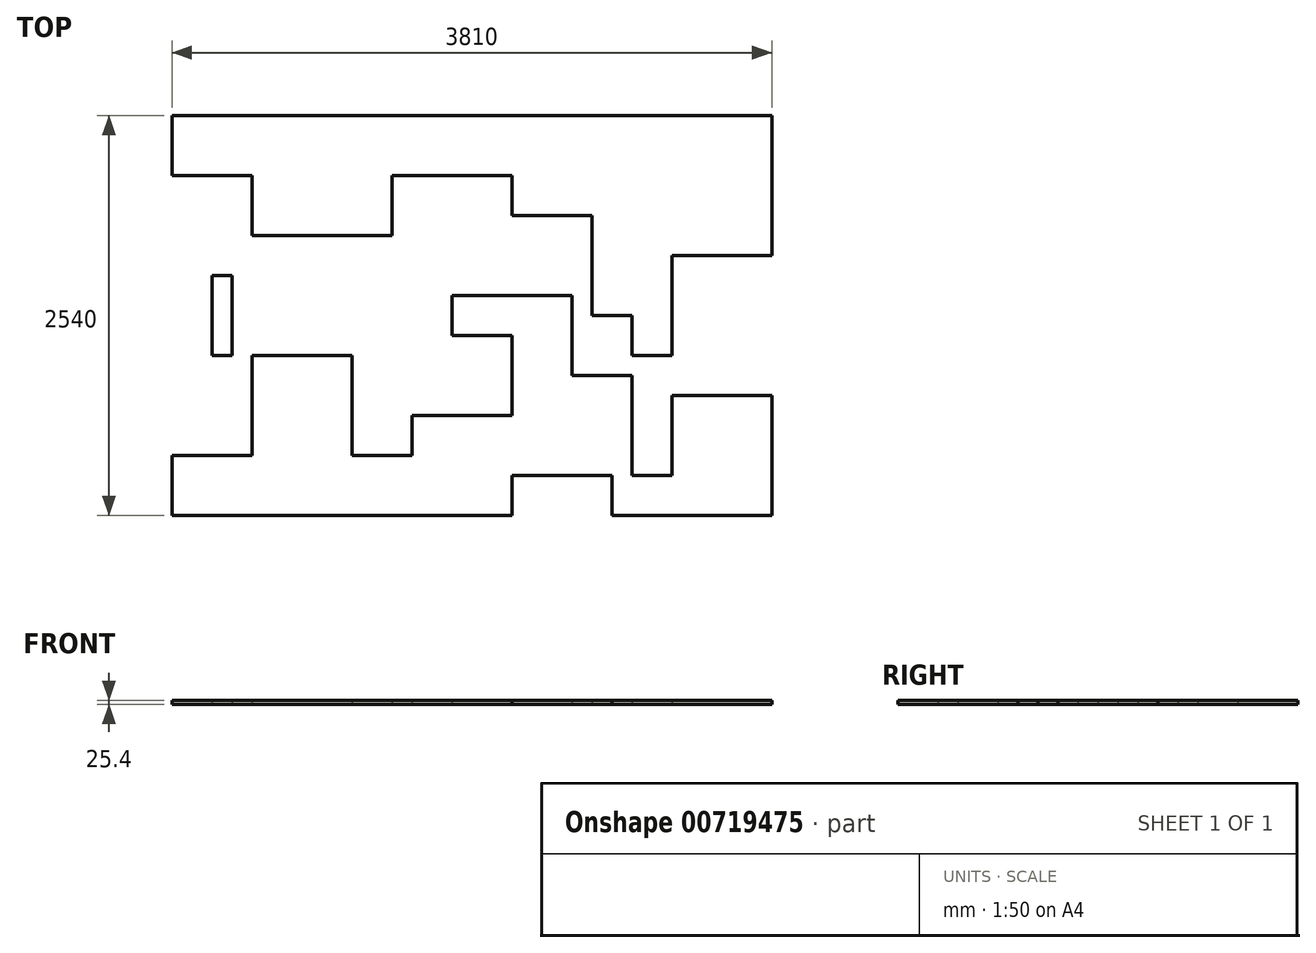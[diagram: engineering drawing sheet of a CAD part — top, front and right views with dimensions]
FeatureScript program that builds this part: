
annotation { "Feature Type Name" : "Feature", "Feature Type Description" : "" }
export const myFeature = defineFeature(function(context is Context, id is Id, definition is map)
    precondition{}
    {
        {
            var Q0;
            Q0=qCreatedBy(makeId("Top.planeOp"),FACE);
            var sketch = newSketch(context, id + "F0", { "sketchPlane" : qUnion([Q0])});
            skLineSegment(sketch, "E0", {"start": v(-1270, 1270) * mm, "end": v(-1270, -1270) * mm, "construction": true});
            skLineSegment(sketch, "E1", {"start": v(-1270, -1270) * mm, "end": v(2540, -1270) * mm, "construction": true});
            skLineSegment(sketch, "E2.0.2.0", {"start": v(889, -1016) * mm, "end": v(2540, -1016) * mm, "construction": true});
            skLineSegment(sketch, "E2.0.3.0", {"start": v(-1270, -889) * mm, "end": v(-762, -889) * mm, "construction": true});
            skLineSegment(sketch, "E2.0.8.0", {"start": v(-1270, -254) * mm, "end": v(-889, -254) * mm, "construction": true});
            skLineSegment(sketch, "E2.0.9.0", {"start": v(508, -127) * mm, "end": v(1270, -127) * mm, "construction": true});
            skLineSegment(sketch, "E2.0.10.0", {"start": v(-127, 0) * mm, "end": v(254, 0) * mm, "construction": true});
            skLineSegment(sketch, "E2.0.11.0", {"start": v(508, 127) * mm, "end": v(1270, 127) * mm, "construction": true});
            skLineSegment(sketch, "E2.0.12.0", {"start": v(-1016, 254) * mm, "end": v(-762, 254) * mm, "construction": true});
            skLineSegment(sketch, "E2.0.13.0", {"start": v(-762, 381) * mm, "end": v(508, 381) * mm, "construction": true});
            skLineSegment(sketch, "E2.0.14.0", {"start": v(-1270, 508) * mm, "end": v(508, 508) * mm, "construction": true});
            skLineSegment(sketch, "E2.0.17.0", {"start": v(-1270, 889) * mm, "end": v(-762, 889) * mm, "construction": true});
            skLineSegment(sketch, "E2.direction1", {"start": v(-1270, -1270) * mm, "end": v(-1244.6, -1270) * mm, "construction": true});
            skLineSegment(sketch, "E2.direction2", {"start": v(-1270, -1270) * mm, "end": v(-1270, -1143) * mm, "construction": true});
            skLineSegment(sketch, "E3.0.0.20", {"start": v(-1270, 1270) * mm, "end": v(2540, 1270) * mm, "construction": true});
            skLineSegment(sketch, "E4.4.0.0", {"start": v(-762, 1270) * mm, "end": v(-762, -1270) * mm, "construction": true});
            skLineSegment(sketch, "E4.9.0.0", {"start": v(-127, 1270) * mm, "end": v(-127, 508) * mm, "construction": true});
            skLineSegment(sketch, "E4.11.0.0", {"start": v(127, 1270) * mm, "end": v(127, 508) * mm, "construction": true});
            skLineSegment(sketch, "E4.14.0.0", {"start": v(508, 889) * mm, "end": v(508, -1270) * mm, "construction": true});
            skLineSegment(sketch, "E4.17.0.0", {"start": v(889, 1270) * mm, "end": v(889, 127) * mm, "construction": true});
            skLineSegment(sketch, "E4.direction1", {"start": v(-1270, -1270) * mm, "end": v(-1143, -1270) * mm, "construction": true});
            skLineSegment(sketch, "E5.0.20.0", {"start": v(1270, 635) * mm, "end": v(1270, -381) * mm, "construction": true});
            skLineSegment(sketch, "E6.0.21.0", {"start": v(1397, 1270) * mm, "end": v(1397, -254) * mm, "construction": true});
            skLineSegment(sketch, "E6.0.25.0", {"start": v(1905, 1270) * mm, "end": v(1905, -127) * mm, "construction": true});
            skLineSegment(sketch, "E6.0.28.0", {"start": v(2286, 381) * mm, "end": v(2286, -508) * mm, "construction": true});
            skLineSegment(sketch, "E6.0.30.0", {"start": v(2540, 1270) * mm, "end": v(2540, -1270) * mm, "construction": true});
            skLineSegment(sketch, "E7.bottom", {"start": v(-1270, 1270) * mm, "end": v(-762, 1270) * mm});
            skLineSegment(sketch, "E7.top", {"start": v(-1270, 889) * mm, "end": v(-762, 889) * mm});
            skLineSegment(sketch, "E7.left", {"start": v(-1270, 1270) * mm, "end": v(-1270, 889) * mm});
            skLineSegment(sketch, "E7.right", {"start": v(-762, 1270) * mm, "end": v(-762, 889) * mm});
            skLineSegment(sketch, "E8.bottom", {"start": v(-762, 1270) * mm, "end": v(-127, 1270) * mm});
            skLineSegment(sketch, "E8.top", {"start": v(-762, 508) * mm, "end": v(-127, 508) * mm});
            skLineSegment(sketch, "E8.left", {"start": v(-762, 1270) * mm, "end": v(-762, 508) * mm});
            skLineSegment(sketch, "E8.right", {"start": v(-127, 1270) * mm, "end": v(-127, 508) * mm});
            skLineSegment(sketch, "E9.bottom", {"start": v(-127, 762) * mm, "end": v(127, 762) * mm});
            skLineSegment(sketch, "E9.top", {"start": v(-127, 1270) * mm, "end": v(127, 1270) * mm});
            skLineSegment(sketch, "E9.left", {"start": v(-127, 762) * mm, "end": v(-127, 1270) * mm});
            skLineSegment(sketch, "E9.right", {"start": v(127, 762) * mm, "end": v(127, 1270) * mm});
            skLineSegment(sketch, "E10.bottom", {"start": v(127, 1270) * mm, "end": v(889, 1270) * mm});
            skLineSegment(sketch, "E10.top", {"start": v(127, 889) * mm, "end": v(889, 889) * mm});
            skLineSegment(sketch, "E10.left", {"start": v(127, 1270) * mm, "end": v(127, 889) * mm});
            skLineSegment(sketch, "E10.right", {"start": v(889, 1270) * mm, "end": v(889, 889) * mm});
            skLineSegment(sketch, "E11.bottom", {"start": v(889, 1270) * mm, "end": v(1397, 1270) * mm});
            skLineSegment(sketch, "E11.top", {"start": v(889, 635) * mm, "end": v(1397, 635) * mm});
            skLineSegment(sketch, "E11.left", {"start": v(889, 1270) * mm, "end": v(889, 635) * mm});
            skLineSegment(sketch, "E11.right", {"start": v(1397, 1270) * mm, "end": v(1397, 635) * mm});
            skLineSegment(sketch, "E12.bottom", {"start": v(508, 889) * mm, "end": v(127, 889) * mm});
            skLineSegment(sketch, "E12.top", {"start": v(508, 508) * mm, "end": v(127, 508) * mm});
            skLineSegment(sketch, "E12.left", {"start": v(508, 889) * mm, "end": v(508, 508) * mm});
            skLineSegment(sketch, "E12.right", {"start": v(127, 889) * mm, "end": v(127, 508) * mm});
            skLineSegment(sketch, "E13.bottom", {"start": v(889, 254) * mm, "end": v(508, 254) * mm});
            skLineSegment(sketch, "E13.top", {"start": v(889, 889) * mm, "end": v(508, 889) * mm});
            skLineSegment(sketch, "E13.left", {"start": v(889, 254) * mm, "end": v(889, 889) * mm});
            skLineSegment(sketch, "E13.right", {"start": v(508, 254) * mm, "end": v(508, 889) * mm});
            skLineSegment(sketch, "E14.bottom", {"start": v(1397, 889) * mm, "end": v(1905, 889) * mm});
            skLineSegment(sketch, "E14.top", {"start": v(1397, 1270) * mm, "end": v(1905, 1270) * mm});
            skLineSegment(sketch, "E14.left", {"start": v(1397, 889) * mm, "end": v(1397, 1270) * mm});
            skLineSegment(sketch, "E14.right", {"start": v(1905, 889) * mm, "end": v(1905, 1270) * mm});
            skLineSegment(sketch, "E15.bottom", {"start": v(1905, 1270) * mm, "end": v(2540, 1270) * mm});
            skLineSegment(sketch, "E15.top", {"start": v(1905, 381) * mm, "end": v(2540, 381) * mm});
            skLineSegment(sketch, "E15.left", {"start": v(1905, 1270) * mm, "end": v(1905, 381) * mm});
            skLineSegment(sketch, "E15.right", {"start": v(2540, 1270) * mm, "end": v(2540, 381) * mm});
            skLineSegment(sketch, "E16.top", {"start": v(1397, 0) * mm, "end": v(1905, 0) * mm});
            skLineSegment(sketch, "E16.left", {"start": v(1397, 889) * mm, "end": v(1397, 0) * mm});
            skLineSegment(sketch, "E16.right", {"start": v(1905, 889) * mm, "end": v(1905, 0) * mm});
            skLineSegment(sketch, "E17.bottom", {"start": v(1905, 381) * mm, "end": v(2286, 381) * mm});
            skLineSegment(sketch, "E17.top", {"start": v(1905, -254) * mm, "end": v(2286, -254) * mm});
            skLineSegment(sketch, "E17.left", {"start": v(1905, 381) * mm, "end": v(1905, -254) * mm});
            skLineSegment(sketch, "E17.right", {"start": v(2286, 381) * mm, "end": v(2286, -254) * mm});
            skLineSegment(sketch, "E18.bottom", {"start": v(2286, 381) * mm, "end": v(2540, 381) * mm});
            skLineSegment(sketch, "E18.top", {"start": v(2286, -508) * mm, "end": v(2540, -508) * mm});
            skLineSegment(sketch, "E18.left", {"start": v(2286, 381) * mm, "end": v(2286, -508) * mm});
            skLineSegment(sketch, "E18.right", {"start": v(2540, 381) * mm, "end": v(2540, -508) * mm});
            skLineSegment(sketch, "E19.bottom", {"start": v(2286, -254) * mm, "end": v(1651, -254) * mm});
            skLineSegment(sketch, "E19.top", {"start": v(2286, -508) * mm, "end": v(1651, -508) * mm});
            skLineSegment(sketch, "E19.left", {"start": v(2286, -254) * mm, "end": v(2286, -508) * mm});
            skLineSegment(sketch, "E19.right", {"start": v(1651, -254) * mm, "end": v(1651, -508) * mm});
            skLineSegment(sketch, "E20.bottom", {"start": v(2540, -508) * mm, "end": v(1905, -508) * mm});
            skLineSegment(sketch, "E20.top", {"start": v(2540, -1016) * mm, "end": v(1905, -1016) * mm});
            skLineSegment(sketch, "E20.left", {"start": v(2540, -508) * mm, "end": v(2540, -1016) * mm});
            skLineSegment(sketch, "E20.right", {"start": v(1905, -508) * mm, "end": v(1905, -1016) * mm});
            skLineSegment(sketch, "E21.bottom", {"start": v(2540, -1270) * mm, "end": v(2032, -1270) * mm});
            skLineSegment(sketch, "E21.top", {"start": v(2540, -1016) * mm, "end": v(2032, -1016) * mm});
            skLineSegment(sketch, "E21.left", {"start": v(2540, -1270) * mm, "end": v(2540, -1016) * mm});
            skLineSegment(sketch, "E21.right", {"start": v(2032, -1270) * mm, "end": v(2032, -1016) * mm});
            skLineSegment(sketch, "E22.bottom", {"start": v(1651, -508) * mm, "end": v(1905, -508) * mm});
            skLineSegment(sketch, "E22.top", {"start": v(1651, -1016) * mm, "end": v(1905, -1016) * mm});
            skLineSegment(sketch, "E22.left", {"start": v(1651, -508) * mm, "end": v(1651, -1016) * mm});
            skLineSegment(sketch, "E23.bottom", {"start": v(1524, -1016) * mm, "end": v(2032, -1016) * mm});
            skLineSegment(sketch, "E23.top", {"start": v(1524, -1270) * mm, "end": v(2032, -1270) * mm});
            skLineSegment(sketch, "E23.left", {"start": v(1524, -1016) * mm, "end": v(1524, -1270) * mm});
            skLineSegment(sketch, "E23.right", {"start": v(2032, -1016) * mm, "end": v(2032, -1270) * mm});
            skLineSegment(sketch, "E24.bottom", {"start": v(1651, -1016) * mm, "end": v(889, -1016) * mm});
            skLineSegment(sketch, "E24.top", {"start": v(1651, -381) * mm, "end": v(889, -381) * mm});
            skLineSegment(sketch, "E24.left", {"start": v(1651, -1016) * mm, "end": v(1651, -381) * mm});
            skLineSegment(sketch, "E24.right", {"start": v(889, -1016) * mm, "end": v(889, -381) * mm});
            skLineSegment(sketch, "E25.bottom", {"start": v(889, -1016) * mm, "end": v(1524, -1016) * mm});
            skLineSegment(sketch, "E25.top", {"start": v(889, -1270) * mm, "end": v(1524, -1270) * mm});
            skLineSegment(sketch, "E25.left", {"start": v(889, -1016) * mm, "end": v(889, -1270) * mm});
            skLineSegment(sketch, "E26.bottom", {"start": v(889, -1270) * mm, "end": v(508, -1270) * mm});
            skLineSegment(sketch, "E26.top", {"start": v(889, -635) * mm, "end": v(508, -635) * mm});
            skLineSegment(sketch, "E26.left", {"start": v(889, -1270) * mm, "end": v(889, -635) * mm});
            skLineSegment(sketch, "E26.right", {"start": v(508, -1270) * mm, "end": v(508, -635) * mm});
            skLineSegment(sketch, "E27.bottom", {"start": v(508, -1270) * mm, "end": v(-254, -1270) * mm});
            skLineSegment(sketch, "E27.top", {"start": v(508, -889) * mm, "end": v(-254, -889) * mm});
            skLineSegment(sketch, "E27.left", {"start": v(508, -1270) * mm, "end": v(508, -889) * mm});
            skLineSegment(sketch, "E27.right", {"start": v(-254, -1270) * mm, "end": v(-254, -889) * mm});
            skLineSegment(sketch, "E28.bottom", {"start": v(-254, -1270) * mm, "end": v(-762, -1270) * mm});
            skLineSegment(sketch, "E28.top", {"start": v(-254, -635) * mm, "end": v(-762, -635) * mm});
            skLineSegment(sketch, "E28.left", {"start": v(-254, -1270) * mm, "end": v(-254, -635) * mm});
            skLineSegment(sketch, "E28.right", {"start": v(-762, -1270) * mm, "end": v(-762, -635) * mm});
            skLineSegment(sketch, "E29.bottom", {"start": v(-1270, -889) * mm, "end": v(-762, -889) * mm});
            skLineSegment(sketch, "E29.top", {"start": v(-1270, -1270) * mm, "end": v(-762, -1270) * mm});
            skLineSegment(sketch, "E29.left", {"start": v(-1270, -889) * mm, "end": v(-1270, -1270) * mm});
            skLineSegment(sketch, "E29.right", {"start": v(-762, -889) * mm, "end": v(-762, -1270) * mm});
            skLineSegment(sketch, "E30.bottom", {"start": v(-1270, -889) * mm, "end": v(-889, -889) * mm});
            skLineSegment(sketch, "E30.top", {"start": v(-1270, -254) * mm, "end": v(-889, -254) * mm});
            skLineSegment(sketch, "E30.left", {"start": v(-1270, -889) * mm, "end": v(-1270, -254) * mm});
            skLineSegment(sketch, "E30.right", {"start": v(-889, -889) * mm, "end": v(-889, -254) * mm});
            skLineSegment(sketch, "E31.bottom", {"start": v(-762, -889) * mm, "end": v(-889, -889) * mm});
            skLineSegment(sketch, "E31.top", {"start": v(-762, 254) * mm, "end": v(-889, 254) * mm});
            skLineSegment(sketch, "E31.left", {"start": v(-762, -889) * mm, "end": v(-762, 254) * mm});
            skLineSegment(sketch, "E31.right", {"start": v(-889, -889) * mm, "end": v(-889, 254) * mm});
            skLineSegment(sketch, "E32.bottom", {"start": v(-127, 508) * mm, "end": v(127, 508) * mm});
            skLineSegment(sketch, "E32.left", {"start": v(-127, 508) * mm, "end": v(-127, 762) * mm});
            skLineSegment(sketch, "E32.right", {"start": v(127, 508) * mm, "end": v(127, 762) * mm});
            skLineSegment(sketch, "E33.bottom", {"start": v(-762, 508) * mm, "end": v(508, 508) * mm});
            skLineSegment(sketch, "E33.top", {"start": v(-762, 381) * mm, "end": v(508, 381) * mm});
            skLineSegment(sketch, "E33.left", {"start": v(-762, 508) * mm, "end": v(-762, 381) * mm});
            skLineSegment(sketch, "E33.right", {"start": v(508, 508) * mm, "end": v(508, 381) * mm});
            skLineSegment(sketch, "E34.bottom", {"start": v(1397, 635) * mm, "end": v(1270, 635) * mm});
            skLineSegment(sketch, "E34.top", {"start": v(1397, -381) * mm, "end": v(1270, -381) * mm});
            skLineSegment(sketch, "E34.left", {"start": v(1397, 635) * mm, "end": v(1397, -381) * mm});
            skLineSegment(sketch, "E34.right", {"start": v(1270, 635) * mm, "end": v(1270, -381) * mm});
            skLineSegment(sketch, "E35.bottom", {"start": v(1651, 0) * mm, "end": v(1397, 0) * mm});
            skLineSegment(sketch, "E35.top", {"start": v(1651, -381) * mm, "end": v(1397, -381) * mm});
            skLineSegment(sketch, "E35.left", {"start": v(1651, 0) * mm, "end": v(1651, -381) * mm});
            skLineSegment(sketch, "E35.right", {"start": v(1397, 0) * mm, "end": v(1397, -381) * mm});
            skLineSegment(sketch, "E36.bottom", {"start": v(1270, 635) * mm, "end": v(889, 635) * mm});
            skLineSegment(sketch, "E36.top", {"start": v(1270, 127) * mm, "end": v(889, 127) * mm});
            skLineSegment(sketch, "E36.left", {"start": v(1270, 635) * mm, "end": v(1270, 127) * mm});
            skLineSegment(sketch, "E36.right", {"start": v(889, 635) * mm, "end": v(889, 127) * mm});
            skLineSegment(sketch, "E37.bottom", {"start": v(1270, 127) * mm, "end": v(508, 127) * mm});
            skLineSegment(sketch, "E37.top", {"start": v(1270, -127) * mm, "end": v(508, -127) * mm});
            skLineSegment(sketch, "E37.left", {"start": v(1270, 127) * mm, "end": v(1270, -127) * mm});
            skLineSegment(sketch, "E37.right", {"start": v(508, 127) * mm, "end": v(508, -127) * mm});
            skLineSegment(sketch, "E38.bottom", {"start": v(508, 254) * mm, "end": v(889, 254) * mm});
            skLineSegment(sketch, "E38.top", {"start": v(508, 127) * mm, "end": v(889, 127) * mm});
            skLineSegment(sketch, "E38.left", {"start": v(508, 254) * mm, "end": v(508, 127) * mm});
            skLineSegment(sketch, "E38.right", {"start": v(889, 254) * mm, "end": v(889, 127) * mm});
            skLineSegment(sketch, "E39.bottom", {"start": v(508, -127) * mm, "end": v(889, -127) * mm});
            skLineSegment(sketch, "E39.top", {"start": v(508, -635) * mm, "end": v(889, -635) * mm});
            skLineSegment(sketch, "E39.left", {"start": v(508, -127) * mm, "end": v(508, -635) * mm});
            skLineSegment(sketch, "E39.right", {"start": v(889, -127) * mm, "end": v(889, -635) * mm});
            skLineSegment(sketch, "E40.bottom", {"start": v(-762, 508) * mm, "end": v(-1270, 508) * mm});
            skLineSegment(sketch, "E40.top", {"start": v(-762, 889) * mm, "end": v(-1270, 889) * mm});
            skLineSegment(sketch, "E40.left", {"start": v(-762, 508) * mm, "end": v(-762, 889) * mm});
            skLineSegment(sketch, "E40.right", {"start": v(-1270, 508) * mm, "end": v(-1270, 889) * mm});
            skLineSegment(sketch, "E41.bottom", {"start": v(-1270, 508) * mm, "end": v(-1016, 508) * mm});
            skLineSegment(sketch, "E41.top", {"start": v(-1270, -254) * mm, "end": v(-1016, -254) * mm});
            skLineSegment(sketch, "E41.left", {"start": v(-1270, 508) * mm, "end": v(-1270, -254) * mm});
            skLineSegment(sketch, "E41.right", {"start": v(-1016, 508) * mm, "end": v(-1016, -254) * mm});
            skLineSegment(sketch, "E42.bottom", {"start": v(-1016, 508) * mm, "end": v(-762, 508) * mm});
            skLineSegment(sketch, "E42.top", {"start": v(-1016, 254) * mm, "end": v(-762, 254) * mm});
            skLineSegment(sketch, "E42.left", {"start": v(-1016, 508) * mm, "end": v(-1016, 254) * mm});
            skLineSegment(sketch, "E42.right", {"start": v(-762, 508) * mm, "end": v(-762, 254) * mm});
            skLineSegment(sketch, "E43.bottom", {"start": v(-762, 381) * mm, "end": v(-127, 381) * mm});
            skLineSegment(sketch, "E43.top", {"start": v(-762, -254) * mm, "end": v(-127, -254) * mm});
            skLineSegment(sketch, "E43.left", {"start": v(-762, 381) * mm, "end": v(-762, -254) * mm});
            skLineSegment(sketch, "E43.right", {"start": v(-127, 381) * mm, "end": v(-127, -254) * mm});
            skLineSegment(sketch, "E44.bottom", {"start": v(508, 0) * mm, "end": v(-127, 0) * mm});
            skLineSegment(sketch, "E44.top", {"start": v(508, 381) * mm, "end": v(-127, 381) * mm});
            skLineSegment(sketch, "E44.left", {"start": v(508, 0) * mm, "end": v(508, 381) * mm});
            skLineSegment(sketch, "E44.right", {"start": v(-127, 0) * mm, "end": v(-127, 381) * mm});
            skLineSegment(sketch, "E45.bottom", {"start": v(-127, 0) * mm, "end": v(254, 0) * mm});
            skLineSegment(sketch, "E45.top", {"start": v(-127, -508) * mm, "end": v(254, -508) * mm});
            skLineSegment(sketch, "E45.left", {"start": v(-127, 0) * mm, "end": v(-127, -508) * mm});
            skLineSegment(sketch, "E45.right", {"start": v(254, 0) * mm, "end": v(254, -508) * mm});
            skLineSegment(sketch, "E46.bottom", {"start": v(508, -635) * mm, "end": v(254, -635) * mm});
            skLineSegment(sketch, "E46.top", {"start": v(508, 0) * mm, "end": v(254, 0) * mm});
            skLineSegment(sketch, "E46.left", {"start": v(508, -635) * mm, "end": v(508, 0) * mm});
            skLineSegment(sketch, "E46.right", {"start": v(254, -635) * mm, "end": v(254, 0) * mm});
            skLineSegment(sketch, "E47.top", {"start": v(-762, -635) * mm, "end": v(-127, -635) * mm});
            skLineSegment(sketch, "E47.left", {"start": v(-762, -254) * mm, "end": v(-762, -635) * mm});
            skLineSegment(sketch, "E47.right", {"start": v(-127, -254) * mm, "end": v(-127, -635) * mm});
            skLineSegment(sketch, "E48.bottom", {"start": v(-127, -635) * mm, "end": v(-254, -635) * mm});
            skLineSegment(sketch, "E48.top", {"start": v(-127, -889) * mm, "end": v(-254, -889) * mm});
            skLineSegment(sketch, "E48.left", {"start": v(-127, -635) * mm, "end": v(-127, -889) * mm});
            skLineSegment(sketch, "E48.right", {"start": v(-254, -635) * mm, "end": v(-254, -889) * mm});
            skLineSegment(sketch, "E49.bottom", {"start": v(254, -635) * mm, "end": v(508, -635) * mm});
            skLineSegment(sketch, "E49.top", {"start": v(254, -889) * mm, "end": v(508, -889) * mm});
            skLineSegment(sketch, "E49.left", {"start": v(254, -635) * mm, "end": v(254, -889) * mm});
            skLineSegment(sketch, "E49.right", {"start": v(508, -635) * mm, "end": v(508, -889) * mm});
            skLineSegment(sketch, "E50.trimOffspring", {"start": v(-889, 254) * mm, "end": v(-889, -889) * mm, "construction": true});
            skLineSegment(sketch, "E51.trimOffspring", {"start": v(127, 889) * mm, "end": v(889, 889) * mm, "construction": true});
            skLineSegment(sketch, "E52.trimOffspring", {"start": v(-254, -635) * mm, "end": v(-254, -1270) * mm, "construction": true});
            skLineSegment(sketch, "E53.trimOffspring", {"start": v(-127, 762) * mm, "end": v(127, 762) * mm, "construction": true});
            skLineSegment(sketch, "E54.trimOffspring", {"start": v(889, 635) * mm, "end": v(1397, 635) * mm, "construction": true});
            skLineSegment(sketch, "E55.trimOffspring", {"start": v(-1016, 508) * mm, "end": v(-1016, 254) * mm, "construction": true});
            skLineSegment(sketch, "E56.trimOffspring", {"start": v(-762, -254) * mm, "end": v(-127, -254) * mm, "construction": true});
            skLineSegment(sketch, "E57.trimOffspring", {"start": v(-127, -508) * mm, "end": v(254, -508) * mm, "construction": true});
            skLineSegment(sketch, "E58.trimOffspring", {"start": v(-762, -635) * mm, "end": v(-127, -635) * mm, "construction": true});
            skLineSegment(sketch, "E59.trimOffspring", {"start": v(-127, 381) * mm, "end": v(-127, -889) * mm, "construction": true});
            skLineSegment(sketch, "E60.trimOffspring", {"start": v(254, 0) * mm, "end": v(254, -889) * mm, "construction": true});
            skLineSegment(sketch, "E61.trimOffspring", {"start": v(508, 254) * mm, "end": v(889, 254) * mm, "construction": true});
            skLineSegment(sketch, "E62.trimOffspring", {"start": v(-254, -889) * mm, "end": v(508, -889) * mm, "construction": true});
            skLineSegment(sketch, "E63.trimOffspring", {"start": v(1905, 381) * mm, "end": v(2540, 381) * mm, "construction": true});
            skLineSegment(sketch, "E64.trimOffspring", {"start": v(254, -635) * mm, "end": v(889, -635) * mm, "construction": true});
            skLineSegment(sketch, "E65.trimOffspring", {"start": v(1397, 0) * mm, "end": v(1905, 0) * mm, "construction": true});
            skLineSegment(sketch, "E66.trimOffspring", {"start": v(889, -127) * mm, "end": v(889, -1270) * mm, "construction": true});
            skLineSegment(sketch, "E67.trimOffspring", {"start": v(1651, -508) * mm, "end": v(2540, -508) * mm, "construction": true});
            skLineSegment(sketch, "E68.trimOffspring", {"start": v(889, -381) * mm, "end": v(1651, -381) * mm, "construction": true});
            skLineSegment(sketch, "E69.trimOffspring", {"start": v(1397, 889) * mm, "end": v(1905, 889) * mm, "construction": true});
            skLineSegment(sketch, "E70.trimOffspring", {"start": v(1651, -254) * mm, "end": v(2286, -254) * mm, "construction": true});
            skLineSegment(sketch, "E71.trimOffspring", {"start": v(1524, -1016) * mm, "end": v(1524, -1270) * mm, "construction": true});
            skLineSegment(sketch, "E72.trimOffspring", {"start": v(2032, -1016) * mm, "end": v(2032, -1270) * mm, "construction": true});
            skLineSegment(sketch, "E73.trimOffspring", {"start": v(1905, -508) * mm, "end": v(1905, -1016) * mm, "construction": true});
            skLineSegment(sketch, "E74.trimOffspring", {"start": v(1651, 0) * mm, "end": v(1651, -1016) * mm, "construction": true});
            skSolve(sketch);
        }
        {
            var Q0;
            Q0=makeQuery(id+"F0.imprint","IMPRINT",FACE,{"disambiguationData":[TD([[makeQuery(id+"F0.imprint","IMPRINT",EDGE,{"derivedFrom":sQuery(id+"F0.wireOp",EDGE,"E7.bottom")}),-1.0]])]});
            extrude(context, id + "F1", {"entities" : qUnion([Q0]), "depth" : 25.4 * mm, "offsetDistance" : 25.4 * mm});
        }
        {
            var Q0;
            Q0 = qSketchRegion(id + "FHIruazjRhK974Y_0", true);
            var Q1;
            Q1=makeQuery(id+"F0.imprint","IMPRINT",FACE,{"disambiguationData":[TD([[makeQuery(id+"F0.imprint","IMPRINT",EDGE,{"derivedFrom":sQuery(id+"F0.wireOp",EDGE,"E8.bottom")}),-1.0]])]});
            var Q2;
            Q2=makeQuery(id+"F0.imprint","IMPRINT",FACE,{"disambiguationData":[TD([[makeQuery(id+"F0.imprint","IMPRINT",EDGE,{"derivedFrom":sQuery(id+"F0.wireOp",EDGE,"E9.top")}),-1.0]])]});
            var Q3;
            Q3=makeQuery(id+"F0.imprint","IMPRINT",FACE,{"disambiguationData":[TD([[makeQuery(id+"F0.imprint","IMPRINT",EDGE,{"derivedFrom":sQuery(id+"F0.wireOp",EDGE,"E10.bottom")}),-1.0]])]});
            var Q4;
            Q4=makeQuery(id+"F0.imprint","IMPRINT",FACE,{"disambiguationData":[TD([[makeQuery(id+"F0.imprint","IMPRINT",EDGE,{"derivedFrom":sQuery(id+"F0.wireOp",EDGE,"E11.bottom")}),-1.0]])]});
            var Q5;
            Q5=makeQuery(id+"F0.imprint","IMPRINT",FACE,{"disambiguationData":[TD([[makeQuery(id+"F0.imprint","IMPRINT",EDGE,{"derivedFrom":sQuery(id+"F0.wireOp",EDGE,"E14.top")}),-1.0]])]});
            var Q6;
            Q6=makeQuery(id+"F0.imprint","IMPRINT",FACE,{"disambiguationData":[TD([[makeQuery(id+"F0.imprint","IMPRINT",EDGE,{"derivedFrom":sQuery(id+"F0.wireOp",EDGE,"E15.bottom")}),-1.0]])]});
            var Q7;
            Q7=makeQuery(id+"F0.imprint","IMPRINT",FACE,{"disambiguationData":[TD([[makeQuery(id+"F0.imprint","IMPRINT",EDGE,{"derivedFrom":sQuery(id+"F0.wireOp",EDGE,"E40.top")}),1.0]])]});
            var Q8;
            {var subQ0=sQuery(id+"F0.wireOp",EDGE,"E33.right");Q8=makeQuery(id+"F0.imprint","IMPRINT",FACE,{"disambiguationData":[TD([[makeQuery(id+"F0.imprint","IMPRINT",EDGE,{"derivedFrom":subQ0}),-1.0]])]});}
            var Q9;
            Q9=makeQuery(id+"F0.imprint","IMPRINT",FACE,{"disambiguationData":[TD([[makeQuery(id+"F0.imprint","IMPRINT",EDGE,{"derivedFrom":sQuery(id+"F0.wireOp",EDGE,"E9.bottom")}),-1.0]])]});
            var Q10;
            Q10=makeQuery(id+"F0.imprint","IMPRINT",FACE,{"disambiguationData":[TD([[makeQuery(id+"F0.imprint","IMPRINT",EDGE,{"derivedFrom":sQuery(id+"F0.wireOp",EDGE,"E12.bottom")}),1.0]])]});
            var Q11;
            Q11=makeQuery(id+"F0.imprint","IMPRINT",FACE,{"disambiguationData":[TD([[makeQuery(id+"F0.imprint","IMPRINT",EDGE,{"derivedFrom":sQuery(id+"F0.wireOp",EDGE,"E13.top")}),1.0]])]});
            var Q12;
            Q12=makeQuery(id+"F0.imprint","IMPRINT",FACE,{"disambiguationData":[TD([[makeQuery(id+"F0.imprint","IMPRINT",EDGE,{"derivedFrom":sQuery(id+"F0.wireOp",EDGE,"E36.bottom")}),1.0]])]});
            var Q13;
            Q13=makeQuery(id+"F0.imprint","IMPRINT",FACE,{"disambiguationData":[TD([[makeQuery(id+"F0.imprint","IMPRINT",EDGE,{"derivedFrom":sQuery(id+"F0.wireOp",EDGE,"E34.bottom")}),1.0]])]});
            var Q14;
            Q14=makeQuery(id+"F0.imprint","IMPRINT",FACE,{"disambiguationData":[TD([[makeQuery(id+"F0.imprint","IMPRINT",EDGE,{"derivedFrom":sQuery(id+"F0.wireOp",EDGE,"E14.bottom")}),-1.0]])]});
            var Q15;
            {var subQ5=sQuery(id+"F0.wireOp",EDGE,"E17.bottom");Q15=makeQuery(id+"F0.imprint","IMPRINT",FACE,{"disambiguationData":[TD([[makeQuery(id+"F0.imprint","IMPRINT",EDGE,{"derivedFrom":subQ5}),-1.0]])]});}
            var Q16;
            Q16=makeQuery(id+"F0.imprint","IMPRINT",FACE,{"disambiguationData":[TD([[makeQuery(id+"F0.imprint","IMPRINT",EDGE,{"derivedFrom":sQuery(id+"F0.wireOp",EDGE,"E18.bottom")}),-1.0]])]});
            extrude(context, id + "F2", {"entities" : qUnion([Q0, Q1, Q2, Q3, Q4, Q5, Q6, Q7, Q8, Q9, Q10, Q11, Q12, Q13, Q14, Q15, Q16]), "operationType" : NewBodyOperationType.ADD, "depth" : 25.4 * mm, "offsetDistance" : 25.4 * mm});
        }
        {
            var Q0;
            Q0=makeQuery(id+"F0.imprint","IMPRINT",FACE,{"disambiguationData":[TD([[makeQuery(id+"F0.imprint","IMPRINT",EDGE,{"derivedFrom":sQuery(id+"F0.wireOp",EDGE,"E41.bottom")}),-1.0]])]});
            var Q1;
            Q1=makeQuery(id+"F0.imprint","IMPRINT",FACE,{"disambiguationData":[TD([[makeQuery(id+"F0.imprint","IMPRINT",EDGE,{"derivedFrom":sQuery(id+"F0.wireOp",EDGE,"E42.bottom")}),-1.0]])]});
            var Q2;
            {var subQ3=sQuery(id+"F0.wireOp",EDGE,"E43.bottom");Q2=makeQuery(id+"F0.imprint","IMPRINT",FACE,{"disambiguationData":[TD([[makeQuery(id+"F0.imprint","IMPRINT",EDGE,{"derivedFrom":subQ3}),-1.0]])]});}
            var Q3;
            {var subQ1=sQuery(id+"F0.wireOp",EDGE,"E44.top");Q3=makeQuery(id+"F0.imprint","IMPRINT",FACE,{"disambiguationData":[TD([[makeQuery(id+"F0.imprint","IMPRINT",EDGE,{"derivedFrom":subQ1}),1.0]])]});}
            var Q4;
            {var subQ0=sQuery(id+"F0.wireOp",EDGE,"E38.bottom");Q4=makeQuery(id+"F0.imprint","IMPRINT",FACE,{"disambiguationData":[TD([[makeQuery(id+"F0.imprint","IMPRINT",EDGE,{"derivedFrom":subQ0}),-1.0]])]});}
            var Q5;
            Q5=makeQuery(id+"F0.imprint","IMPRINT",FACE,{"disambiguationData":[TD([[makeQuery(id+"F0.imprint","IMPRINT",EDGE,{"derivedFrom":sQuery(id+"F0.wireOp",EDGE,"E37.bottom")}),1.0]])]});
            var Q6;
            {var subQ0=sQuery(id+"F0.wireOp",EDGE,"E24.top");Q6=makeQuery(id+"F0.imprint","IMPRINT",FACE,{"disambiguationData":[TD([[makeQuery(id+"F0.imprint","IMPRINT",EDGE,{"derivedFrom":subQ0}),-1.0]])]});}
            var Q7;
            {var subQ3=sQuery(id+"F0.wireOp",EDGE,"E24.bottom");Q7=makeQuery(id+"F0.imprint","IMPRINT",FACE,{"disambiguationData":[TD([[makeQuery(id+"F0.imprint","IMPRINT",EDGE,{"derivedFrom":subQ3}),-1.0]])]});}
            var Q8;
            {var subQ1=sQuery(id+"F0.wireOp",EDGE,"E19.left");Q8=makeQuery(id+"F0.imprint","IMPRINT",FACE,{"disambiguationData":[TD([[makeQuery(id+"F0.imprint","IMPRINT",EDGE,{"derivedFrom":subQ1}),-1.0]])]});}
            var Q9;
            {var subQ1=sQuery(id+"F0.wireOp",EDGE,"E20.left");Q9=makeQuery(id+"F0.imprint","IMPRINT",FACE,{"disambiguationData":[TD([[makeQuery(id+"F0.imprint","IMPRINT",EDGE,{"derivedFrom":subQ1}),-1.0]])]});}
            extrude(context, id + "F3", {"entities" : qUnion([Q0, Q1, Q2, Q3, Q4, Q5, Q6, Q7, Q8, Q9]), "operationType" : NewBodyOperationType.ADD, "depth" : 25.4 * mm, "offsetDistance" : 25.4 * mm});
        }
        {
            var Q0;
            {var subQ3=sQuery(id+"F0.wireOp",EDGE,"E35.bottom");Q0=makeQuery(id+"F0.imprint","IMPRINT",FACE,{"disambiguationData":[TD([[makeQuery(id+"F0.imprint","IMPRINT",EDGE,{"derivedFrom":subQ3}),1.0]])]});}
            var Q1;
            {var subQ0=sQuery(id+"F0.wireOp",EDGE,"E16.top");Q1=makeQuery(id+"F0.imprint","IMPRINT",FACE,{"disambiguationData":[TD([[makeQuery(id+"F0.imprint","IMPRINT",EDGE,{"derivedFrom":subQ0}),-1.0]])]});}
            extrude(context, id + "F4", {"entities" : qUnion([Q0, Q1]), "operationType" : NewBodyOperationType.ADD, "depth" : 25.4 * mm, "offsetDistance" : 25.4 * mm});
        }
        {
            var Q0;
            {var subQ2=sQuery(id+"F0.wireOp",EDGE,"E30.bottom");Q0=makeQuery(id+"F0.imprint","IMPRINT",FACE,{"disambiguationData":[TD([[makeQuery(id+"F0.imprint","IMPRINT",EDGE,{"derivedFrom":subQ2}),1.0]])]});}
            var Q1;
            {var subQ0=sQuery(id+"F0.wireOp",EDGE,"E30.top");Q1=makeQuery(id+"F0.imprint","IMPRINT",FACE,{"disambiguationData":[TD([[makeQuery(id+"F0.imprint","IMPRINT",EDGE,{"derivedFrom":subQ0}),1.0]])]});}
            var Q2;
            {var subQ7=sQuery(id+"F0.wireOp",EDGE,"E31.bottom");Q2=makeQuery(id+"F0.imprint","IMPRINT",FACE,{"disambiguationData":[TD([[makeQuery(id+"F0.imprint","IMPRINT",EDGE,{"derivedFrom":subQ7}),-1.0]])]});}
            var Q3;
            {var subQ2=sQuery(id+"F0.wireOp",EDGE,"E43.top");Q3=makeQuery(id+"F0.imprint","IMPRINT",FACE,{"disambiguationData":[TD([[makeQuery(id+"F0.imprint","IMPRINT",EDGE,{"derivedFrom":subQ2}),-1.0]])]});}
            var Q4;
            {var subQ1=sQuery(id+"F0.wireOp",EDGE,"E45.bottom");Q4=makeQuery(id+"F0.imprint","IMPRINT",FACE,{"disambiguationData":[TD([[makeQuery(id+"F0.imprint","IMPRINT",EDGE,{"derivedFrom":subQ1}),-1.0]])]});}
            var Q5;
            {var subQ5=sQuery(id+"F0.wireOp",EDGE,"E46.top");Q5=makeQuery(id+"F0.imprint","IMPRINT",FACE,{"disambiguationData":[TD([[makeQuery(id+"F0.imprint","IMPRINT",EDGE,{"derivedFrom":subQ5}),1.0]])]});}
            var Q6;
            {var subQ3=sQuery(id+"F0.wireOp",EDGE,"E39.bottom");Q6=makeQuery(id+"F0.imprint","IMPRINT",FACE,{"disambiguationData":[TD([[makeQuery(id+"F0.imprint","IMPRINT",EDGE,{"derivedFrom":subQ3}),-1.0]])]});}
            var Q7;
            {var subQ0=sQuery(id+"F0.wireOp",EDGE,"E25.bottom");Q7=makeQuery(id+"F0.imprint","IMPRINT",FACE,{"disambiguationData":[TD([[makeQuery(id+"F0.imprint","IMPRINT",EDGE,{"derivedFrom":subQ0}),-1.0]])]});}
            var Q8;
            {var subQ0=sQuery(id+"F0.wireOp",EDGE,"E22.bottom");Q8=makeQuery(id+"F0.imprint","IMPRINT",FACE,{"disambiguationData":[TD([[makeQuery(id+"F0.imprint","IMPRINT",EDGE,{"derivedFrom":subQ0}),-1.0]])]});}
            var Q9;
            Q9=makeQuery(id+"F0.imprint","IMPRINT",FACE,{"disambiguationData":[TD([[makeQuery(id+"F0.imprint","IMPRINT",EDGE,{"derivedFrom":sQuery(id+"F0.wireOp",EDGE,"E23.top")}),1.0]])]});
            var Q10;
            Q10=makeQuery(id+"F0.imprint","IMPRINT",FACE,{"disambiguationData":[TD([[makeQuery(id+"F0.imprint","IMPRINT",EDGE,{"derivedFrom":sQuery(id+"F0.wireOp",EDGE,"E21.bottom")}),-1.0]])]});
            extrude(context, id + "F5", {"entities" : qUnion([Q0, Q1, Q2, Q3, Q4, Q5, Q6, Q7, Q8, Q9, Q10]), "operationType" : NewBodyOperationType.ADD, "depth" : 25.4 * mm, "offsetDistance" : 25.4 * mm});
        }
        {
            var Q0;
            Q0=makeQuery(id+"F0.imprint","IMPRINT",FACE,{"disambiguationData":[TD([[makeQuery(id+"F0.imprint","IMPRINT",EDGE,{"derivedFrom":sQuery(id+"F0.wireOp",EDGE,"E29.top")}),1.0]])]});
            var Q1;
            Q1=makeQuery(id+"F0.imprint","IMPRINT",FACE,{"disambiguationData":[TD([[makeQuery(id+"F0.imprint","IMPRINT",EDGE,{"derivedFrom":sQuery(id+"F0.wireOp",EDGE,"E28.bottom")}),-1.0]])]});
            var Q2;
            Q2=makeQuery(id+"F0.imprint","IMPRINT",FACE,{"disambiguationData":[TD([[makeQuery(id+"F0.imprint","IMPRINT",EDGE,{"derivedFrom":sQuery(id+"F0.wireOp",EDGE,"E48.bottom")}),1.0]])]});
            var Q3;
            Q3=makeQuery(id+"F0.imprint","IMPRINT",FACE,{"disambiguationData":[TD([[makeQuery(id+"F0.imprint","IMPRINT",EDGE,{"derivedFrom":sQuery(id+"F0.wireOp",EDGE,"E27.top")}),-1.0]])]});
            var Q4;
            Q4=makeQuery(id+"F0.imprint","IMPRINT",FACE,{"disambiguationData":[TD([[makeQuery(id+"F0.imprint","IMPRINT",EDGE,{"derivedFrom":sQuery(id+"F0.wireOp",EDGE,"E49.bottom")}),-1.0]])]});
            var Q5;
            {var subQ3=sQuery(id+"F0.wireOp",EDGE,"E26.bottom");Q5=makeQuery(id+"F0.imprint","IMPRINT",FACE,{"disambiguationData":[TD([[makeQuery(id+"F0.imprint","IMPRINT",EDGE,{"derivedFrom":subQ3}),-1.0]])]});}
            extrude(context, id + "F6", {"entities" : qUnion([Q0, Q1, Q2, Q3, Q4, Q5]), "operationType" : NewBodyOperationType.ADD, "depth" : 25.4 * mm, "offsetDistance" : 25.4 * mm});
        }
        {
            var Q0;
            Q0=makeQuery(id+"F0.imprint","IMPRINT",FACE,{"disambiguationData":[TD([[makeQuery(id+"F0.imprint","IMPRINT",EDGE,{"derivedFrom":sQuery(id+"F0.wireOp",EDGE,"E27.bottom")}),-1.0]])]});
            extrude(context, id + "F7", {"entities" : qUnion([Q0]), "operationType" : NewBodyOperationType.ADD, "depth" : 25.4 * mm, "offsetDistance" : 25.4 * mm});
        }
    });
